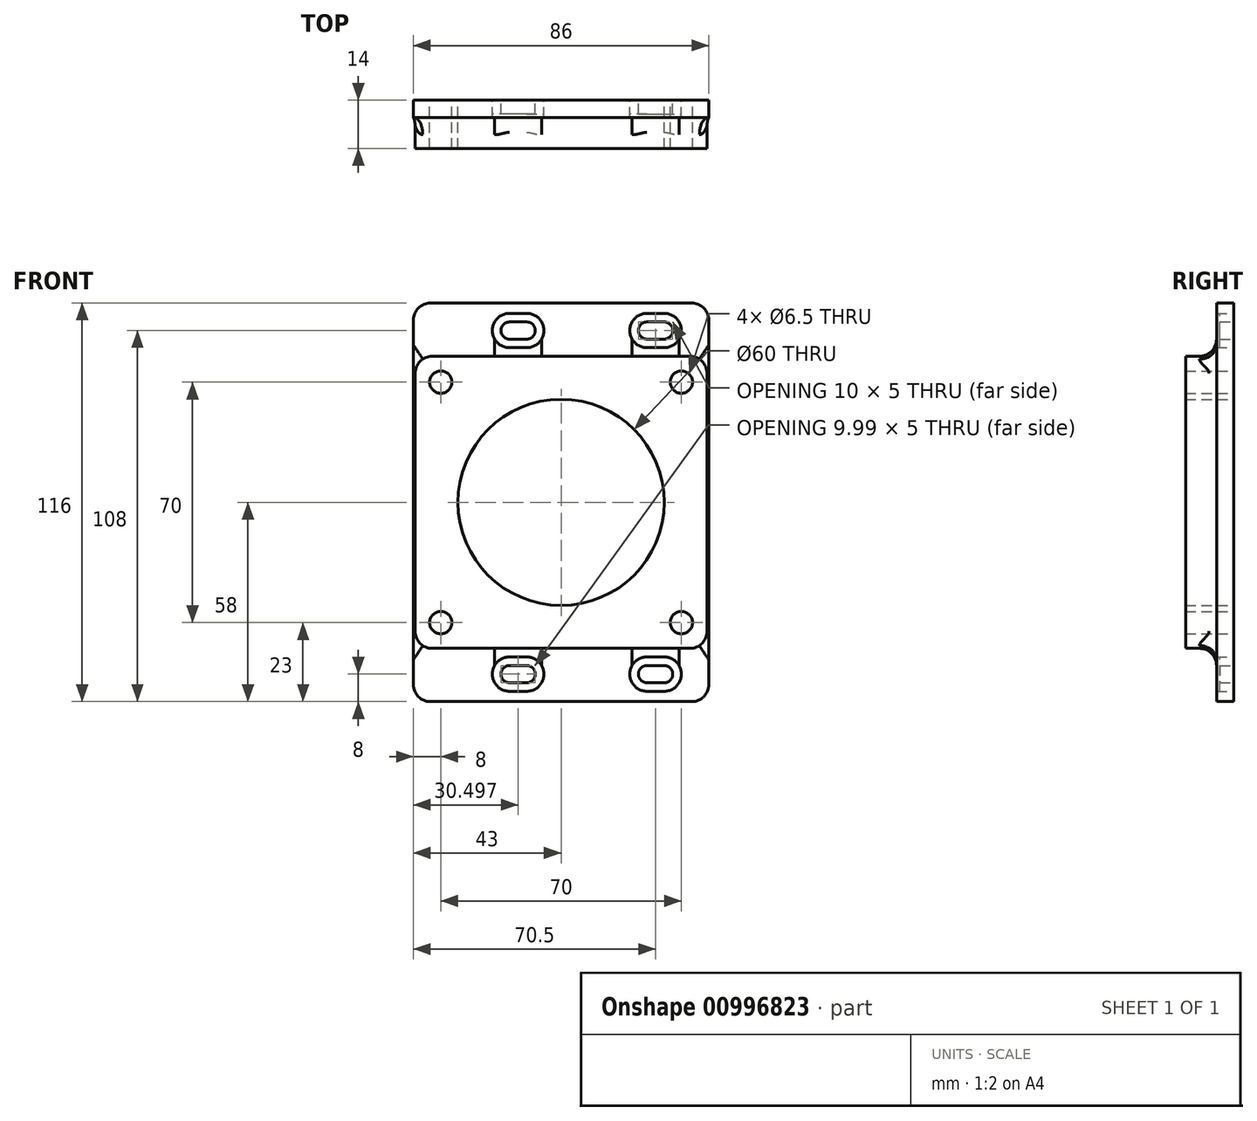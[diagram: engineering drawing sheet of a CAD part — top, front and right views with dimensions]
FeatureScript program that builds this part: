
annotation { "Feature Type Name" : "Feature", "Feature Type Description" : "" }
export const myFeature = defineFeature(function(context is Context, id is Id, definition is map)
    precondition{}
    {
        {
            var Q0;
            Q0=qCreatedBy(makeId("Front.planeOp"),FACE);
            var sketch = newSketch(context, id + "F0", { "sketchPlane" : qUnion([Q0])});
            skLineSegment(sketch, "E0.bottom", {"start": v(43, -58) * mm, "end": v(-43, -58) * mm});
            skLineSegment(sketch, "E0.top", {"start": v(43, 58) * mm, "end": v(-43, 58) * mm});
            skLineSegment(sketch, "E0.left", {"start": v(43, -58) * mm, "end": v(43, 58) * mm});
            skLineSegment(sketch, "E0.right", {"start": v(-43, -58) * mm, "end": v(-43, 58) * mm});
            skPoint(sketch, "E0.middle", {"position": v(0, 0) * mm});
            skArc(sketch, "E1", {"start": v(30, 47.5) * mm, "mid": v(32.5, 50) * mm, "end": v(30, 52.5) * mm});
            skArc(sketch, "E2", {"start": v(27.5, 47.5) * mm, "mid": v(27.5, 47.5) * mm, "end": v(27.5, 47.5) * mm});
            skArc(sketch, "E3", {"start": v(25, 52.5) * mm, "mid": v(22.5, 50) * mm, "end": v(25.01, 47.5) * mm});
            skLineSegment(sketch, "E4", {"start": v(25.01, 47.5) * mm, "end": v(30, 47.5) * mm});
            skLineSegment(sketch, "E5", {"start": v(25, 52.5) * mm, "end": v(30, 52.5) * mm});
            skArc(sketch, "E6", {"start": v(25, 55) * mm, "mid": v(20, 50) * mm, "end": v(25, 45) * mm});
            skLineSegment(sketch, "E7", {"start": v(25, 55) * mm, "end": v(30, 55) * mm});
            skLineSegment(sketch, "E8", {"start": v(25, 45) * mm, "end": v(30, 45) * mm});
            skArc(sketch, "E9.trimOffspring", {"start": v(30, 45) * mm, "mid": v(35, 50) * mm, "end": v(30, 55) * mm});
            skLineSegment(sketch, "E10.MirrorCS", {"start": v(25.01, -47.5) * mm, "end": v(30, -47.5) * mm});
            skArc(sketch, "E11.MirrorCS", {"start": v(27.5, -47.5) * mm, "mid": v(27.5, -47.5) * mm, "end": v(27.5, -47.5) * mm});
            skArc(sketch, "E12.MirrorCS", {"start": v(25, -52.5) * mm, "mid": v(22.5, -50) * mm, "end": v(25.01, -47.5) * mm});
            skLineSegment(sketch, "E13.MirrorCS", {"start": v(25, -45) * mm, "end": v(30, -45) * mm});
            skLineSegment(sketch, "E14.MirrorCS", {"start": v(25, -55) * mm, "end": v(30, -55) * mm});
            skArc(sketch, "E15.MirrorCS", {"start": v(25, -55) * mm, "mid": v(20, -50) * mm, "end": v(25, -45) * mm});
            skLineSegment(sketch, "E16.MirrorCS", {"start": v(25, -52.5) * mm, "end": v(30, -52.5) * mm});
            skArc(sketch, "E17.MirrorCS", {"start": v(30, -45) * mm, "mid": v(35, -50) * mm, "end": v(30, -55) * mm});
            skArc(sketch, "E18.MirrorCS", {"start": v(30, -47.5) * mm, "mid": v(32.5, -50) * mm, "end": v(30, -52.5) * mm});
            skArc(sketch, "E19.MirrorCS", {"start": v(-12.5, 47.5) * mm, "mid": v(-12.5, 47.5) * mm, "end": v(-12.5, 47.5) * mm});
            skLineSegment(sketch, "E20.MirrorCS", {"start": v(-10, 55) * mm, "end": v(-15, 55) * mm});
            skLineSegment(sketch, "E21.MirrorCS", {"start": v(-10, 45) * mm, "end": v(-15, 45) * mm});
            skArc(sketch, "E22.MirrorCS", {"start": v(-10, 55) * mm, "mid": v(-5, 50) * mm, "end": v(-10, 45) * mm});
            skArc(sketch, "E23.MirrorCS", {"start": v(-15, 45) * mm, "mid": v(-20, 50) * mm, "end": v(-15, 55) * mm});
            skArc(sketch, "E24.MirrorCS", {"start": v(-15, 47.5) * mm, "mid": v(-17.5, 50) * mm, "end": v(-15, 52.5) * mm});
            skArc(sketch, "E25.MirrorCS", {"start": v(-10, 52.5) * mm, "mid": v(-7.5, 50) * mm, "end": v(-10.01, 47.5) * mm});
            skLineSegment(sketch, "E26.MirrorCS", {"start": v(-10.01, 47.5) * mm, "end": v(-15, 47.5) * mm});
            skLineSegment(sketch, "E27.MirrorCS", {"start": v(-10, 52.5) * mm, "end": v(-15, 52.5) * mm});
            skArc(sketch, "E28.MirrorCS", {"start": v(-12.5, -47.5) * mm, "mid": v(-12.5, -47.5) * mm, "end": v(-12.5, -47.5) * mm});
            skArc(sketch, "E29.MirrorCS", {"start": v(-15, -45) * mm, "mid": v(-20, -50) * mm, "end": v(-15, -55) * mm});
            skLineSegment(sketch, "E30.MirrorCS", {"start": v(-10, -52.5) * mm, "end": v(-15, -52.5) * mm});
            skLineSegment(sketch, "E31.MirrorCS", {"start": v(-10, -55) * mm, "end": v(-15, -55) * mm});
            skArc(sketch, "E32.MirrorCS", {"start": v(-10, -55) * mm, "mid": v(-5, -50) * mm, "end": v(-10, -45) * mm});
            skLineSegment(sketch, "E33.MirrorCS", {"start": v(-10.01, -47.5) * mm, "end": v(-15, -47.5) * mm});
            skArc(sketch, "E34.MirrorCS", {"start": v(-15, -47.5) * mm, "mid": v(-17.5, -50) * mm, "end": v(-15, -52.5) * mm});
            skArc(sketch, "E35.MirrorCS", {"start": v(-10, -52.5) * mm, "mid": v(-7.5, -50) * mm, "end": v(-10.01, -47.5) * mm});
            skLineSegment(sketch, "E36.MirrorCS", {"start": v(-10, -45) * mm, "end": v(-15, -45) * mm});
            skSolve(sketch);
        }
        {
            var Q0;
            Q0=qCreatedBy(makeId("Front.planeOp"),FACE);
            var sketch = newSketch(context, id + "F1", { "sketchPlane" : qUnion([Q0])});
            skLineSegment(sketch, "E37.bottom", {"start": v(37.5, 42.5) * mm, "end": v(-37.5, 42.5) * mm});
            skLineSegment(sketch, "E37.top", {"start": v(37.5, -42.5) * mm, "end": v(-37.5, -42.5) * mm});
            skLineSegment(sketch, "E37.left", {"start": v(42.5, 37.5) * mm, "end": v(42.5, -37.5) * mm});
            skLineSegment(sketch, "E37.right", {"start": v(-42.5, 37.5) * mm, "end": v(-42.5, -37.5) * mm});
            skPoint(sketch, "E37.middle", {"position": v(0, 0) * mm});
            skCircle(sketch, "E38", {"center": v(-35, 35) * mm, "radius": 3.25 * mm});
            skCircle(sketch, "E39.MirrorC", {"center": v(35, 35) * mm, "radius": 3.25 * mm});
            skCircle(sketch, "E40.MirrorC", {"center": v(-35, -35) * mm, "radius": 3.25 * mm});
            skCircle(sketch, "E41.MirrorC", {"center": v(35, -35) * mm, "radius": 3.25 * mm});
            skPoint(sketch, "E42.visualSharp", {"position": v(-42.5, 42.5) * mm});
            skArc(sketch, "E42.filletArc", {"start": v(-37.5, 42.5) * mm, "mid": v(-41.04, 41.04) * mm, "end": v(-42.5, 37.5) * mm});
            skPoint(sketch, "E43.visualSharp", {"position": v(42.5, 42.5) * mm});
            skArc(sketch, "E43.filletArc", {"start": v(42.5, 37.5) * mm, "mid": v(41.04, 41.04) * mm, "end": v(37.5, 42.5) * mm});
            skPoint(sketch, "E44.visualSharp", {"position": v(42.5, -42.5) * mm});
            skArc(sketch, "E44.filletArc", {"start": v(37.5, -42.5) * mm, "mid": v(41.04, -41.04) * mm, "end": v(42.5, -37.5) * mm});
            skPoint(sketch, "E45.visualSharp", {"position": v(-42.5, -42.5) * mm});
            skArc(sketch, "E45.filletArc", {"start": v(-42.5, -37.5) * mm, "mid": v(-41.04, -41.04) * mm, "end": v(-37.5, -42.5) * mm});
            skCircle(sketch, "E46", {"center": v(0, 0) * mm, "radius": 30 * mm});
            skSolve(sketch);
        }
        {
            var Q0;
            Q0=makeQuery(id+"F1.imprint","IMPRINT",FACE,{"disambiguationData":[TD([[makeQuery(id+"F1.imprint","IMPRINT",EDGE,{"derivedFrom":sQuery(id+"F1.wireOp",EDGE,"E37.bottom")}),1.0]])]});
            extrude(context, id + "F2", {"entities" : qUnion([Q0]), "depth" : 14 * mm, "offsetDistance" : 25 * mm});
        }
        {
            var Q0;
            Q0=makeQuery(id+"F0.imprint","IMPRINT",FACE,{"disambiguationData":[TD([[makeQuery(id+"F0.imprint","IMPRINT",EDGE,{"derivedFrom":sQuery(id+"F0.wireOp",EDGE,"E0.bottom")}),-1.0]])]});
            extrude(context, id + "F3", {"entities" : qUnion([Q0]), "operationType" : NewBodyOperationType.ADD, "depth" : 5 * mm, "offsetDistance" : 25 * mm});
        }
        {
            var Q0;
            {var subQ0=sQuery(id+"F0.wireOp",EDGE,"E12.MirrorCS");Q0=makeQuery(id+"F0.imprint","IMPRINT",FACE,{"disambiguationData":[TD([[makeQuery(id+"F0.imprint","IMPRINT",EDGE,{"derivedFrom":subQ0}),1.0]])]});}
            var Q1;
            {var subQ0=sQuery(id+"F0.wireOp",EDGE,"E28.MirrorCS");Q1=makeQuery(id+"F0.imprint","IMPRINT",FACE,{"disambiguationData":[TD([[makeQuery(id+"F0.imprint","IMPRINT",EDGE,{"derivedFrom":subQ0}),-1.0]])]});}
            var Q2;
            {var subQ0=sQuery(id+"F0.wireOp",EDGE,"E19.MirrorCS");Q2=makeQuery(id+"F0.imprint","IMPRINT",FACE,{"disambiguationData":[TD([[makeQuery(id+"F0.imprint","IMPRINT",EDGE,{"derivedFrom":subQ0}),1.0]])]});}
            var Q3;
            {var subQ1=sQuery(id+"F0.wireOp",EDGE,"E1");Q3=makeQuery(id+"F0.imprint","IMPRINT",FACE,{"disambiguationData":[TD([[makeQuery(id+"F0.imprint","IMPRINT",EDGE,{"derivedFrom":subQ1}),-1.0]])]});}
            extrude(context, id + "F4", {"entities" : qUnion([Q0, Q1, Q2, Q3]), "operationType" : NewBodyOperationType.ADD, "depth" : 4 * mm, "offsetDistance" : 25 * mm});
        }
        {
            var Q0;
            Q0=makeQuery(id+"F3.boolean.opBoolean","SPLIT",FACE,{"disambiguationData":[TD([makeQuery(id+"F2.opExtrude","SWEPT_FACE",FACE,{"disambiguationData":[OSD([sQuery(id+"F1.wireOp",EDGE,"E39.MirrorC")])]})])],"derivedFrom":makeQuery(id+"F3.opExtrude","CAP_FACE",FACE,{"disambiguationData":[OSD([sQuery(id+"F0.wireOp",EDGE,"E0.bottom"),sQuery(id+"F0.wireOp",EDGE,"E0.top"),sQuery(id+"F0.wireOp",EDGE,"E0.left"),sQuery(id+"F0.wireOp",EDGE,"E0.right"),sQuery(id+"F0.wireOp",EDGE,"E6"),sQuery(id+"F0.wireOp",EDGE,"E7"),sQuery(id+"F0.wireOp",EDGE,"E8"),sQuery(id+"F0.wireOp",EDGE,"E9.trimOffspring"),sQuery(id+"F0.wireOp",EDGE,"E13.MirrorCS"),sQuery(id+"F0.wireOp",EDGE,"E14.MirrorCS"),sQuery(id+"F0.wireOp",EDGE,"E15.MirrorCS"),sQuery(id+"F0.wireOp",EDGE,"E17.MirrorCS"),sQuery(id+"F0.wireOp",EDGE,"E20.MirrorCS"),sQuery(id+"F0.wireOp",EDGE,"E21.MirrorCS"),sQuery(id+"F0.wireOp",EDGE,"E22.MirrorCS"),sQuery(id+"F0.wireOp",EDGE,"E23.MirrorCS"),sQuery(id+"F0.wireOp",EDGE,"E29.MirrorCS"),sQuery(id+"F0.wireOp",EDGE,"E31.MirrorCS"),sQuery(id+"F0.wireOp",EDGE,"E32.MirrorCS"),sQuery(id+"F0.wireOp",EDGE,"E36.MirrorCS")])],"isStart":false})});
            var Q1;
            Q1=makeQuery(id+"F3.boolean.opBoolean","SPLIT",FACE,{"disambiguationData":[TD([makeQuery(id+"F2.opExtrude","SWEPT_FACE",FACE,{"disambiguationData":[OSD([sQuery(id+"F1.wireOp",EDGE,"E38")])]})])],"derivedFrom":makeQuery(id+"F3.opExtrude","CAP_FACE",FACE,{"disambiguationData":[OSD([sQuery(id+"F0.wireOp",EDGE,"E0.bottom"),sQuery(id+"F0.wireOp",EDGE,"E0.top"),sQuery(id+"F0.wireOp",EDGE,"E0.left"),sQuery(id+"F0.wireOp",EDGE,"E0.right"),sQuery(id+"F0.wireOp",EDGE,"E6"),sQuery(id+"F0.wireOp",EDGE,"E7"),sQuery(id+"F0.wireOp",EDGE,"E8"),sQuery(id+"F0.wireOp",EDGE,"E9.trimOffspring"),sQuery(id+"F0.wireOp",EDGE,"E13.MirrorCS"),sQuery(id+"F0.wireOp",EDGE,"E14.MirrorCS"),sQuery(id+"F0.wireOp",EDGE,"E15.MirrorCS"),sQuery(id+"F0.wireOp",EDGE,"E17.MirrorCS"),sQuery(id+"F0.wireOp",EDGE,"E20.MirrorCS"),sQuery(id+"F0.wireOp",EDGE,"E21.MirrorCS"),sQuery(id+"F0.wireOp",EDGE,"E22.MirrorCS"),sQuery(id+"F0.wireOp",EDGE,"E23.MirrorCS"),sQuery(id+"F0.wireOp",EDGE,"E29.MirrorCS"),sQuery(id+"F0.wireOp",EDGE,"E31.MirrorCS"),sQuery(id+"F0.wireOp",EDGE,"E32.MirrorCS"),sQuery(id+"F0.wireOp",EDGE,"E36.MirrorCS")])],"isStart":false})});
            var Q2;
            Q2=makeQuery(id+"F3.boolean.opBoolean","SPLIT",FACE,{"disambiguationData":[TD([makeQuery(id+"F2.opExtrude","SWEPT_FACE",FACE,{"disambiguationData":[OSD([sQuery(id+"F1.wireOp",EDGE,"E41.MirrorC")])]})])],"derivedFrom":makeQuery(id+"F3.opExtrude","CAP_FACE",FACE,{"disambiguationData":[OSD([sQuery(id+"F0.wireOp",EDGE,"E0.bottom"),sQuery(id+"F0.wireOp",EDGE,"E0.top"),sQuery(id+"F0.wireOp",EDGE,"E0.left"),sQuery(id+"F0.wireOp",EDGE,"E0.right"),sQuery(id+"F0.wireOp",EDGE,"E6"),sQuery(id+"F0.wireOp",EDGE,"E7"),sQuery(id+"F0.wireOp",EDGE,"E8"),sQuery(id+"F0.wireOp",EDGE,"E9.trimOffspring"),sQuery(id+"F0.wireOp",EDGE,"E13.MirrorCS"),sQuery(id+"F0.wireOp",EDGE,"E14.MirrorCS"),sQuery(id+"F0.wireOp",EDGE,"E15.MirrorCS"),sQuery(id+"F0.wireOp",EDGE,"E17.MirrorCS"),sQuery(id+"F0.wireOp",EDGE,"E20.MirrorCS"),sQuery(id+"F0.wireOp",EDGE,"E21.MirrorCS"),sQuery(id+"F0.wireOp",EDGE,"E22.MirrorCS"),sQuery(id+"F0.wireOp",EDGE,"E23.MirrorCS"),sQuery(id+"F0.wireOp",EDGE,"E29.MirrorCS"),sQuery(id+"F0.wireOp",EDGE,"E31.MirrorCS"),sQuery(id+"F0.wireOp",EDGE,"E32.MirrorCS"),sQuery(id+"F0.wireOp",EDGE,"E36.MirrorCS")])],"isStart":false})});
            var Q3;
            Q3=makeQuery(id+"F3.boolean.opBoolean","SPLIT",FACE,{"disambiguationData":[TD([makeQuery(id+"F2.opExtrude","SWEPT_FACE",FACE,{"disambiguationData":[OSD([sQuery(id+"F1.wireOp",EDGE,"E40.MirrorC")])]})])],"derivedFrom":makeQuery(id+"F3.opExtrude","CAP_FACE",FACE,{"disambiguationData":[OSD([sQuery(id+"F0.wireOp",EDGE,"E0.bottom"),sQuery(id+"F0.wireOp",EDGE,"E0.top"),sQuery(id+"F0.wireOp",EDGE,"E0.left"),sQuery(id+"F0.wireOp",EDGE,"E0.right"),sQuery(id+"F0.wireOp",EDGE,"E6"),sQuery(id+"F0.wireOp",EDGE,"E7"),sQuery(id+"F0.wireOp",EDGE,"E8"),sQuery(id+"F0.wireOp",EDGE,"E9.trimOffspring"),sQuery(id+"F0.wireOp",EDGE,"E13.MirrorCS"),sQuery(id+"F0.wireOp",EDGE,"E14.MirrorCS"),sQuery(id+"F0.wireOp",EDGE,"E15.MirrorCS"),sQuery(id+"F0.wireOp",EDGE,"E17.MirrorCS"),sQuery(id+"F0.wireOp",EDGE,"E20.MirrorCS"),sQuery(id+"F0.wireOp",EDGE,"E21.MirrorCS"),sQuery(id+"F0.wireOp",EDGE,"E22.MirrorCS"),sQuery(id+"F0.wireOp",EDGE,"E23.MirrorCS"),sQuery(id+"F0.wireOp",EDGE,"E29.MirrorCS"),sQuery(id+"F0.wireOp",EDGE,"E31.MirrorCS"),sQuery(id+"F0.wireOp",EDGE,"E32.MirrorCS"),sQuery(id+"F0.wireOp",EDGE,"E36.MirrorCS")])],"isStart":false})});
            var Q4;
            Q4=makeQuery(id+"F3.boolean.opBoolean","SPLIT",FACE,{"disambiguationData":[TD([makeQuery(id+"F2.opExtrude","SWEPT_FACE",FACE,{"disambiguationData":[OSD([sQuery(id+"F1.wireOp",EDGE,"E46")])]})])],"derivedFrom":makeQuery(id+"F3.opExtrude","CAP_FACE",FACE,{"disambiguationData":[OSD([sQuery(id+"F0.wireOp",EDGE,"E0.bottom"),sQuery(id+"F0.wireOp",EDGE,"E0.top"),sQuery(id+"F0.wireOp",EDGE,"E0.left"),sQuery(id+"F0.wireOp",EDGE,"E0.right"),sQuery(id+"F0.wireOp",EDGE,"E6"),sQuery(id+"F0.wireOp",EDGE,"E7"),sQuery(id+"F0.wireOp",EDGE,"E8"),sQuery(id+"F0.wireOp",EDGE,"E9.trimOffspring"),sQuery(id+"F0.wireOp",EDGE,"E13.MirrorCS"),sQuery(id+"F0.wireOp",EDGE,"E14.MirrorCS"),sQuery(id+"F0.wireOp",EDGE,"E15.MirrorCS"),sQuery(id+"F0.wireOp",EDGE,"E17.MirrorCS"),sQuery(id+"F0.wireOp",EDGE,"E20.MirrorCS"),sQuery(id+"F0.wireOp",EDGE,"E21.MirrorCS"),sQuery(id+"F0.wireOp",EDGE,"E22.MirrorCS"),sQuery(id+"F0.wireOp",EDGE,"E23.MirrorCS"),sQuery(id+"F0.wireOp",EDGE,"E29.MirrorCS"),sQuery(id+"F0.wireOp",EDGE,"E31.MirrorCS"),sQuery(id+"F0.wireOp",EDGE,"E32.MirrorCS"),sQuery(id+"F0.wireOp",EDGE,"E36.MirrorCS")])],"isStart":false})});
            extrude(context, id + "F5", {"entities" : qUnion([Q0, Q1, Q2, Q3, Q4]), "operationType" : NewBodyOperationType.REMOVE, "oppositeDirection" : true, "depth" : 25 * mm, "offsetDistance" : 25 * mm});
        }
        {
            var Q0;
            Q0=makeQuery(id+"F3.opExtrude","SWEPT_EDGE",EDGE,{"disambiguationData":[OSD([sQuery(id+"F0.wireOp",EDGE,"E0.top"),sQuery(id+"F0.wireOp",EDGE,"E0.left")])]});
            var Q1;
            Q1=makeQuery(id+"F3.opExtrude","SWEPT_EDGE",EDGE,{"disambiguationData":[OSD([sQuery(id+"F0.wireOp",EDGE,"E0.top"),sQuery(id+"F0.wireOp",EDGE,"E0.right")])]});
            var Q2;
            Q2=makeQuery(id+"F3.opExtrude","SWEPT_EDGE",EDGE,{"disambiguationData":[OSD([sQuery(id+"F0.wireOp",EDGE,"E0.bottom"),sQuery(id+"F0.wireOp",EDGE,"E0.left")])]});
            var Q3;
            Q3=makeQuery(id+"F3.opExtrude","SWEPT_EDGE",EDGE,{"disambiguationData":[OSD([sQuery(id+"F0.wireOp",EDGE,"E0.bottom"),sQuery(id+"F0.wireOp",EDGE,"E0.right")])]});
            fillet(context, id + "F6", {"entities" : qUnion([Q0, Q1, Q2, Q3]), "tangentPropagation" : true, "radius" : 5 * mm, "defaultsChanged" : false, "vertexSettings" : [], "allowEdgeOverflow" : false});
        }
        {
            var Q0;
            Q0=makeQuery(id+"F3.boolean.opBoolean","INTERSECT",EDGE,{"derivedFrom":[makeQuery(id+"F2.opExtrude","SWEPT_FACE",FACE,{"disambiguationData":[OSD([sQuery(id+"F1.wireOp",EDGE,"E37.top")])]}),makeQuery(id+"F3.opExtrude","CAP_FACE",FACE,{"disambiguationData":[OSD([sQuery(id+"F0.wireOp",EDGE,"E0.bottom"),sQuery(id+"F0.wireOp",EDGE,"E0.top"),sQuery(id+"F0.wireOp",EDGE,"E0.left"),sQuery(id+"F0.wireOp",EDGE,"E0.right"),sQuery(id+"F0.wireOp",EDGE,"E6"),sQuery(id+"F0.wireOp",EDGE,"E7"),sQuery(id+"F0.wireOp",EDGE,"E8"),sQuery(id+"F0.wireOp",EDGE,"E9.trimOffspring"),sQuery(id+"F0.wireOp",EDGE,"E13.MirrorCS"),sQuery(id+"F0.wireOp",EDGE,"E14.MirrorCS"),sQuery(id+"F0.wireOp",EDGE,"E15.MirrorCS"),sQuery(id+"F0.wireOp",EDGE,"E17.MirrorCS"),sQuery(id+"F0.wireOp",EDGE,"E20.MirrorCS"),sQuery(id+"F0.wireOp",EDGE,"E21.MirrorCS"),sQuery(id+"F0.wireOp",EDGE,"E22.MirrorCS"),sQuery(id+"F0.wireOp",EDGE,"E23.MirrorCS"),sQuery(id+"F0.wireOp",EDGE,"E29.MirrorCS"),sQuery(id+"F0.wireOp",EDGE,"E31.MirrorCS"),sQuery(id+"F0.wireOp",EDGE,"E32.MirrorCS"),sQuery(id+"F0.wireOp",EDGE,"E36.MirrorCS")])],"isStart":false})]});
            fillet(context, id + "F7", {"entities" : qUnion([Q0]), "tangentPropagation" : true, "radius" : 5 * mm, "defaultsChanged" : false, "vertexSettings" : [], "allowEdgeOverflow" : false});
        }
    });
